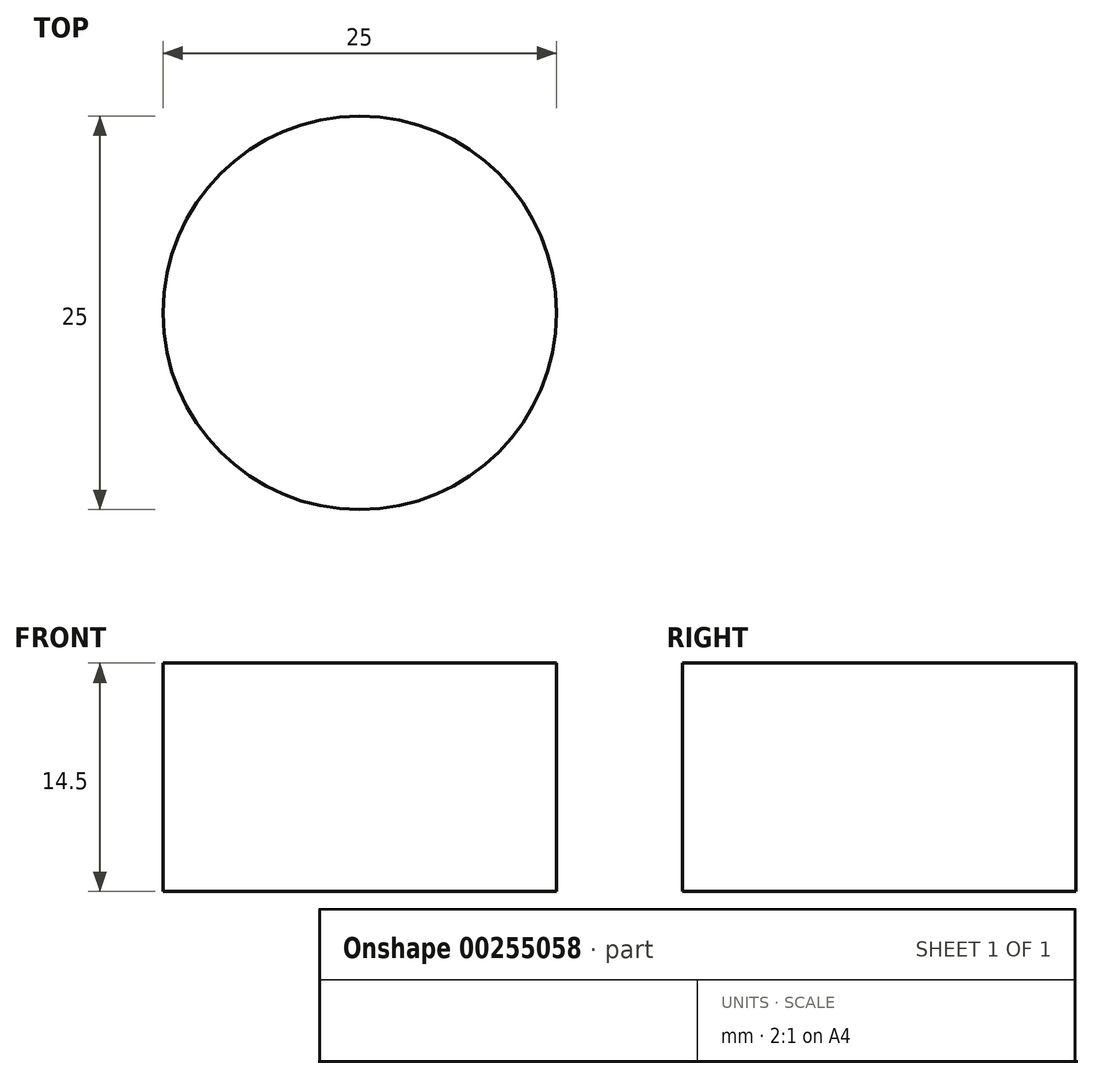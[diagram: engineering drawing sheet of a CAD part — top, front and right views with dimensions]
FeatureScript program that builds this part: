
annotation { "Feature Type Name" : "Feature", "Feature Type Description" : "" }
export const myFeature = defineFeature(function(context is Context, id is Id, definition is map)
    precondition{}
    {
        {
            var Q0;
            Q0=qCreatedBy(makeId("Top.planeOp"),FACE);
            var sketch = newSketch(context, id + "F0", { "sketchPlane" : qUnion([Q0])});
            skCircle(sketch, "E0", {"center": v(0, 0) * mm, "radius": 12.5 * mm});
            skSolve(sketch);
        }
        {
            var Q0;
            Q0=qSketchRegion(id+"F0",true);
            extrude(context, id + "F1", {"entities" : qUnion([Q0]), "depth" : 14.5 * mm});
        }
    });
